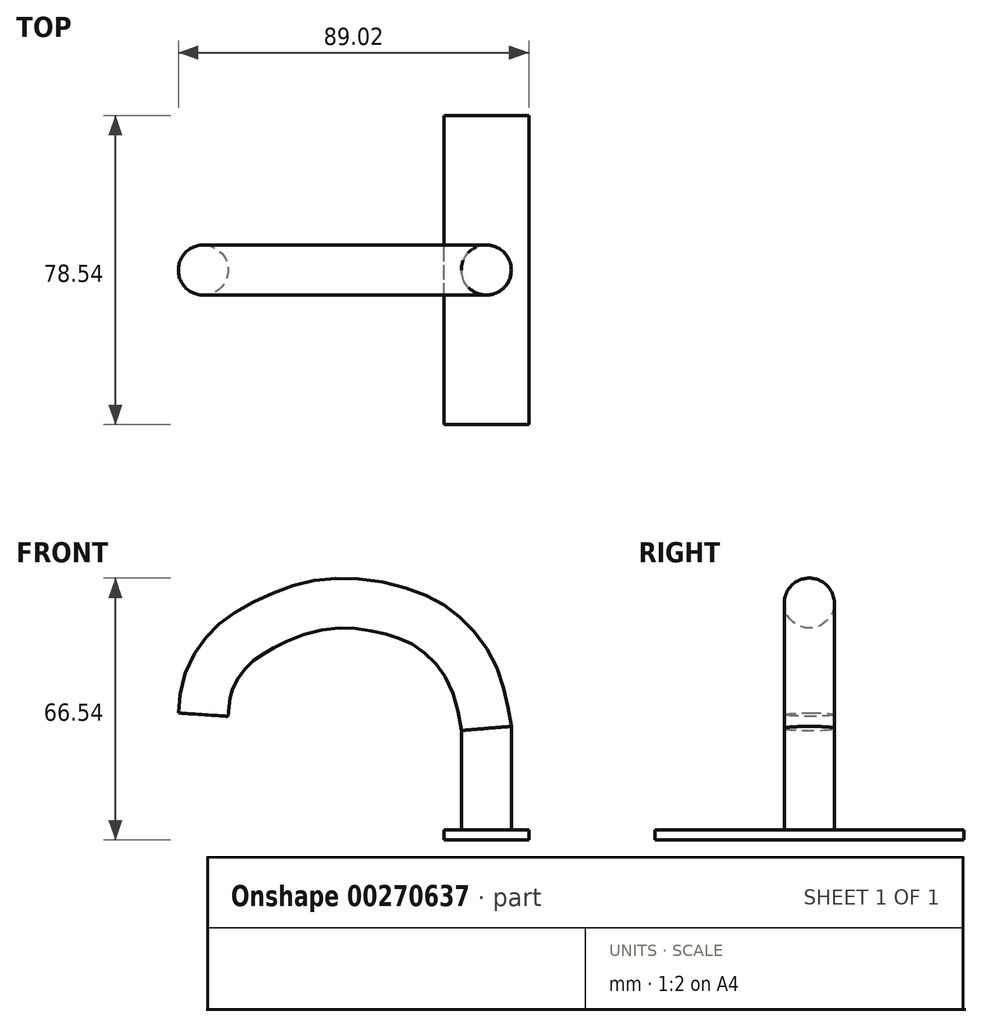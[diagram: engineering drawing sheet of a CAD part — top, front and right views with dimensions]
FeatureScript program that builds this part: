
annotation { "Feature Type Name" : "Feature", "Feature Type Description" : "" }
export const myFeature = defineFeature(function(context is Context, id is Id, definition is map)
    precondition{}
    {
        {
            var Q0;
            Q0=qCreatedBy(makeId("Top.planeOp"),FACE);
            var sketch = newSketch(context, id + "F0", { "sketchPlane" : qUnion([Q0])});
            skCircle(sketch, "E0", {"center": v(0, 0) * mm, "radius": 6.35 * mm});
            skSolve(sketch);
        }
        {
            var Q0;
            Q0=qCreatedBy(makeId("Front.planeOp"),FACE);
            var sketch = newSketch(context, id + "F1", { "sketchPlane" : qUnion([Q0])});
            skLineSegment(sketch, "E1", {"start": v(0, 0) * mm, "end": v(0, 25.8) * mm});
            skFitSpline(sketch, "E2", {"points": [v(0, 25.8) * mm, v(-2.03, 35.58) * mm, v(-5.9, 43.7) * mm, v(-12.17, 50.33) * mm, v(-18.8, 54.2) * mm, v(-31.16, 57.33) * mm, v(-42.4, 57.15) * mm, v(-52.17, 54.2) * mm, v(-61.76, 49.04) * mm, v(-66.55, 44.61) * mm, v(-70.6, 37.6) * mm, v(-71.9, 29.31) * mm], "startDerivative": vector(-17.5, 106.94) * mm, "endDerivative": vector(-6.6, -98.2) * mm});
            skSolve(sketch);
        }
        {
            var Q0;
            Q0=makeQuery(id+"F0.imprint","IMPRINT",FACE,{"disambiguationData":[TD([[makeQuery(id+"F0.imprint","IMPRINT",EDGE,{"derivedFrom":sQuery(id+"F0.wireOp",EDGE,"E0")}),1.0]])]});
            var Q1;
            Q1=sQuery(id+"F1.wireOp",EDGE,"E1");
            var Q2;
            Q2=sQuery(id+"F1.wireOp",EDGE,"E2");
            sweep(context, id + "F2", {"profiles" : qUnion([Q0]), "path" : qUnion([Q1, Q2])});
        }
        {
            var Q0;
            Q0=qCreatedBy(makeId("Top.planeOp"),FACE);
            var sketch = newSketch(context, id + "F3", { "sketchPlane" : qUnion([Q0])});
            skLineSegment(sketch, "E3.bottom", {"start": v(-10.79, -39.27) * mm, "end": v(10.79, -39.27) * mm});
            skLineSegment(sketch, "E3.top", {"start": v(-10.79, 39.27) * mm, "end": v(10.79, 39.27) * mm});
            skLineSegment(sketch, "E3.left", {"start": v(-10.79, -39.27) * mm, "end": v(-10.79, 39.27) * mm});
            skLineSegment(sketch, "E3.right", {"start": v(10.79, -39.27) * mm, "end": v(10.79, 39.27) * mm});
            skPoint(sketch, "E3.middle", {"position": v(0, 0) * mm});
            skSolve(sketch);
        }
        {
            var Q0;
            Q0=makeQuery(id+"F3.imprint","IMPRINT",FACE,{"disambiguationData":[TD([[makeQuery(id+"F3.imprint","IMPRINT",EDGE,{"derivedFrom":sQuery(id+"F3.wireOp",EDGE,"E3.bottom")}),1.0]])]});
            extrude(context, id + "F4", {"entities" : qUnion([Q0]), "operationType" : NewBodyOperationType.ADD, "oppositeDirection" : true, "depth" : 2.54 * mm});
        }
    });
